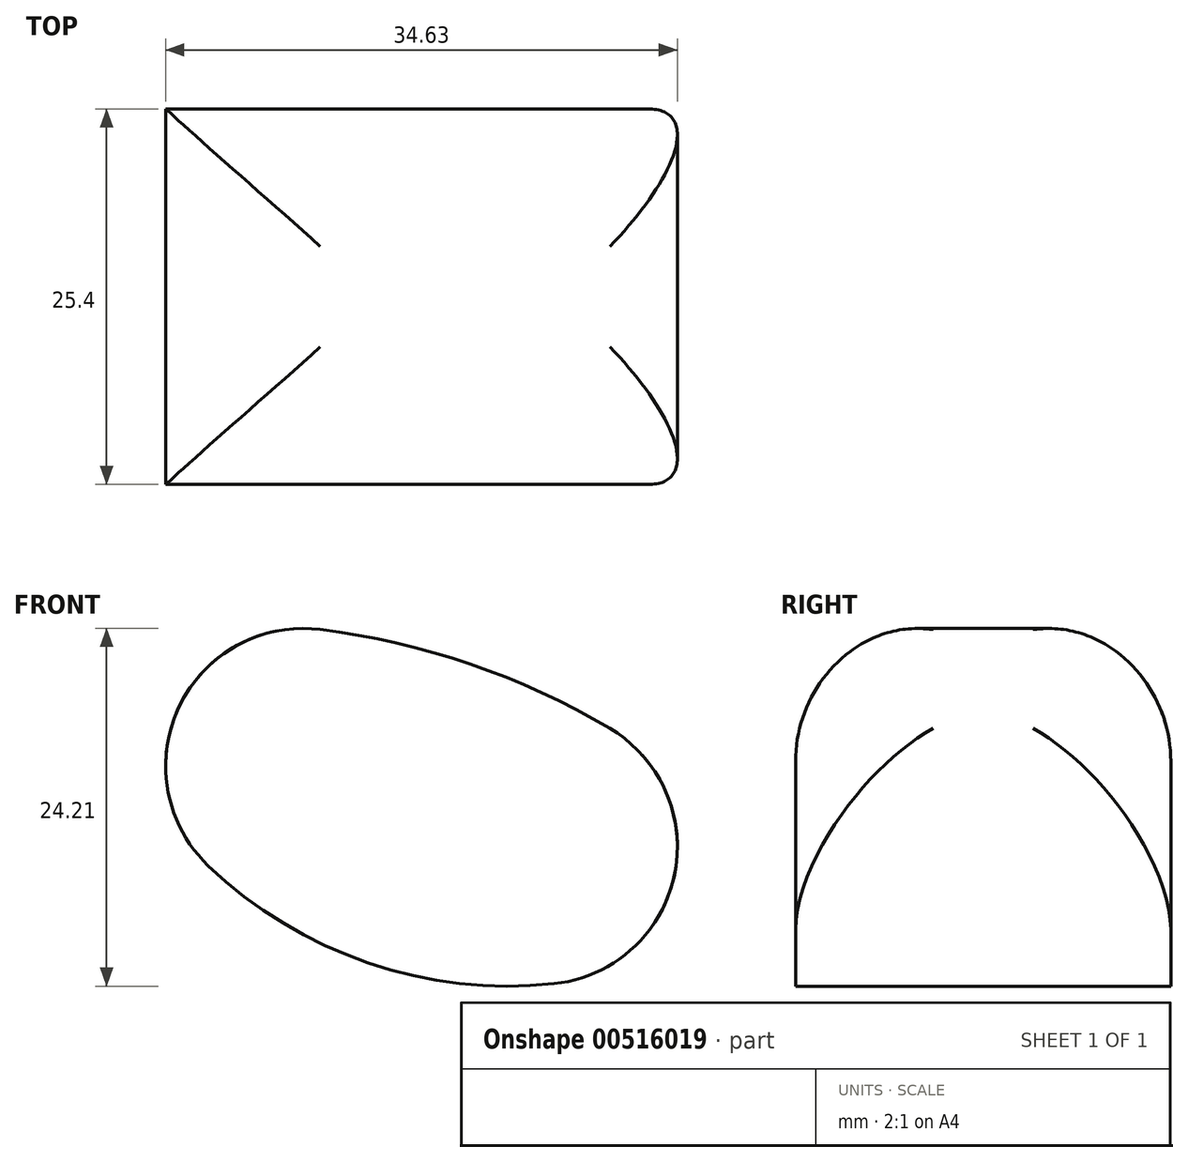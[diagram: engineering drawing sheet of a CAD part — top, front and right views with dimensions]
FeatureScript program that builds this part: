
annotation { "Feature Type Name" : "Feature", "Feature Type Description" : "" }
export const myFeature = defineFeature(function(context is Context, id is Id, definition is map)
    precondition{}
    {
        {
            var Q0;
            Q0=qCreatedBy(makeId("Front.planeOp"),FACE);
            var sketch = newSketch(context, id + "F0", { "sketchPlane" : qUnion([Q0])});
            skCircle(sketch, "E0", {"center": v(0, 0) * mm, "radius": 50.9 * mm});
            skCircle(sketch, "E1", {"center": v(19.05, 55.8) * mm, "radius": 29.42 * mm});
            skSolve(sketch);
        }
        {
            var Q0;
            {var subQ0=sQuery(id+"F0.wireOp",EDGE,"E1");var subQ1=sQuery(id+"F0.wireOp",EDGE,"E0");var subQ2=makeQuery(id+"F0.imprint","INTERSECT",VERTEX,{"disambiguationData":[OD(0.0)],"derivedFrom":[subQ1,subQ0]});Q0=makeQuery(id+"F0.imprint","IMPRINT",FACE,{"disambiguationData":[TD([[makeQuery(id+"F0.imprint","IMPRINT",EDGE,{"disambiguationData":[TD([[subQ2,1.0]])],"derivedFrom":subQ1}),1.0]])]});}
            extrude(context, id + "F1", {"entities" : qUnion([Q0]), "depth" : 25.4 * mm, "offsetDistance" : 25.4 * mm});
        }
        {
            var Q0;
            Q0=makeQuery(id+"F1.opExtrude","SWEPT_FACE",FACE,{"disambiguationData":[OSD([sQuery(id+"F0.wireOp",EDGE,"E0")])]});
            fillet(context, id + "F2", {"entities" : qUnion([Q0]), "radius" : 9.3 * mm, "tangentPropagation" : true, "allowEdgeOverflow" : false});
        }
    });
